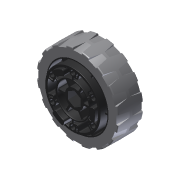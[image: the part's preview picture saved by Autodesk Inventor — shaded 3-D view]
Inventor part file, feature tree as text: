
AUTODESK INVENTOR PART (.ipt)
format: ipt  version: 2013 (Build 170138000, 138)  size: 3,165,696 bytes
history: native  units: in
note: dims shown in document units (in); Inventor stores cm internally (conversion verified against a paired STEP export)
features: fillet x2, imported_body x2, other x1
ambient origin geometry x8: Origin, YZ Plane, XZ Plane, XY Plane, X Axis, Y Axis, Z Axis, Center Point
feature tree (5):
  fillet  "Fillet6"  [1 undecoded]
  other  "217-3238-STEP1"
  fillet  "Fillet7"  [1 undecoded]
  imported_body  "Base1"
  imported_body  "Base2"
note: 2 required parameter values undecoded (feature->parameter linkage not recoverable at this tier; creation-order binding heuristic only, values carry confidence <= 0.55)
